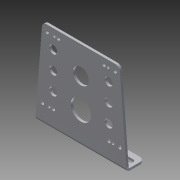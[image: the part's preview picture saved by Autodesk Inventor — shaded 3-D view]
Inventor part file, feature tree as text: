
AUTODESK INVENTOR PART (.ipt)
format: ipt  version: 2014 SP1 (Build 180222100, 222)  size: 119,296 bytes
history: native  units: in
note: dims shown in document units (in); Inventor stores cm internally (conversion verified against a paired STEP export)
features: other x2, plane x1, imported_body x1
ambient origin geometry x8: Origin, YZ Plane, XZ Plane, XY Plane, X Axis, Y Axis, Z Axis, Center Point
bodies: Body1 (feature_tree)
feature tree (4):
  other  "Toughbox-mini_d02"
  other  "Toughbox-mini_d021"
  plane  "Work Plane1"
  imported_body  "Base1"
